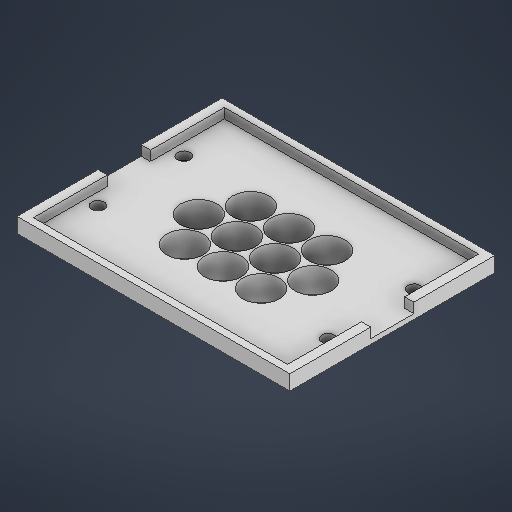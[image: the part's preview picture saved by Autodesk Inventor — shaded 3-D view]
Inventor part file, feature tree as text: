
AUTODESK INVENTOR PART (.ipt)
format: ipt  version: 2025.2 (Build 292293000, 293)  size: 614,912 bytes
history: native  units: mm
features: extrude x5, sketch x5, projected_geometry x2
ambient origin geometry x8: Origin, YZ Plane, XZ Plane, XY Plane, X Axis, Y Axis, Z Axis, Center Point
bodies: Solid1 (feature_tree)
feature tree (12):
  extrude  "Extrusion1"  Depth=1.0mm
  extrude  "Extrusion2"  Depth=1.0mm
  extrude  "Extrusion3"  Depth=1.0mm
  extrude  "Extrusion4"  Depth=24.0mm
  extrude  "Extrusion5"  Depth=3.0mm
  sketch  "Sketch1"  dims[d0=22.0mm d1=1.0mm]
  sketch  "Sketch2"  dims[d2=22.0mm d3=1.0mm]
  sketch  "Sketch3"  dims[d4=22.0mm d5=1.0mm]
  projected_geometry  "Projected Loop1"
  sketch  "Sketch4"  dims[d6=22.0mm d7=24.0mm]
  projected_geometry  "Projected Loop2"
  sketch  "Sketch5"  dims[d8=24.0mm d9=24.0mm d10=24.0mm d11=22.0mm d12=22.0mm d16=22.0mm d17=22.0mm d19=24.0mm d21=24.0mm d22=24.0mm d23=24.0mm d25=26.0mm d27=26.0mm d28=26.0mm d29=26.0mm d30=26.0mm d31=26.0mm d32=26.0mm d33=26.0mm d34=15.0mm d35=0.0mm d36=115.3mm d37=153.4mm d38=5.0mm d39=0.0mm d44=6.0mm d45=3.0mm d46=0.0mm d47=0.0mm d56=7.73mm d57=7.73mm d58=7.73mm d59=7.73mm d60=0.0mm d61=0.0mm d62=7.228mm d63=31.75mm d64=7.228mm d65=7.228mm d66=31.75mm d67=24.0mm d71=24.0mm d72=22.0mm d73=22.0mm d74=0.0mm d75=0.0mm]
